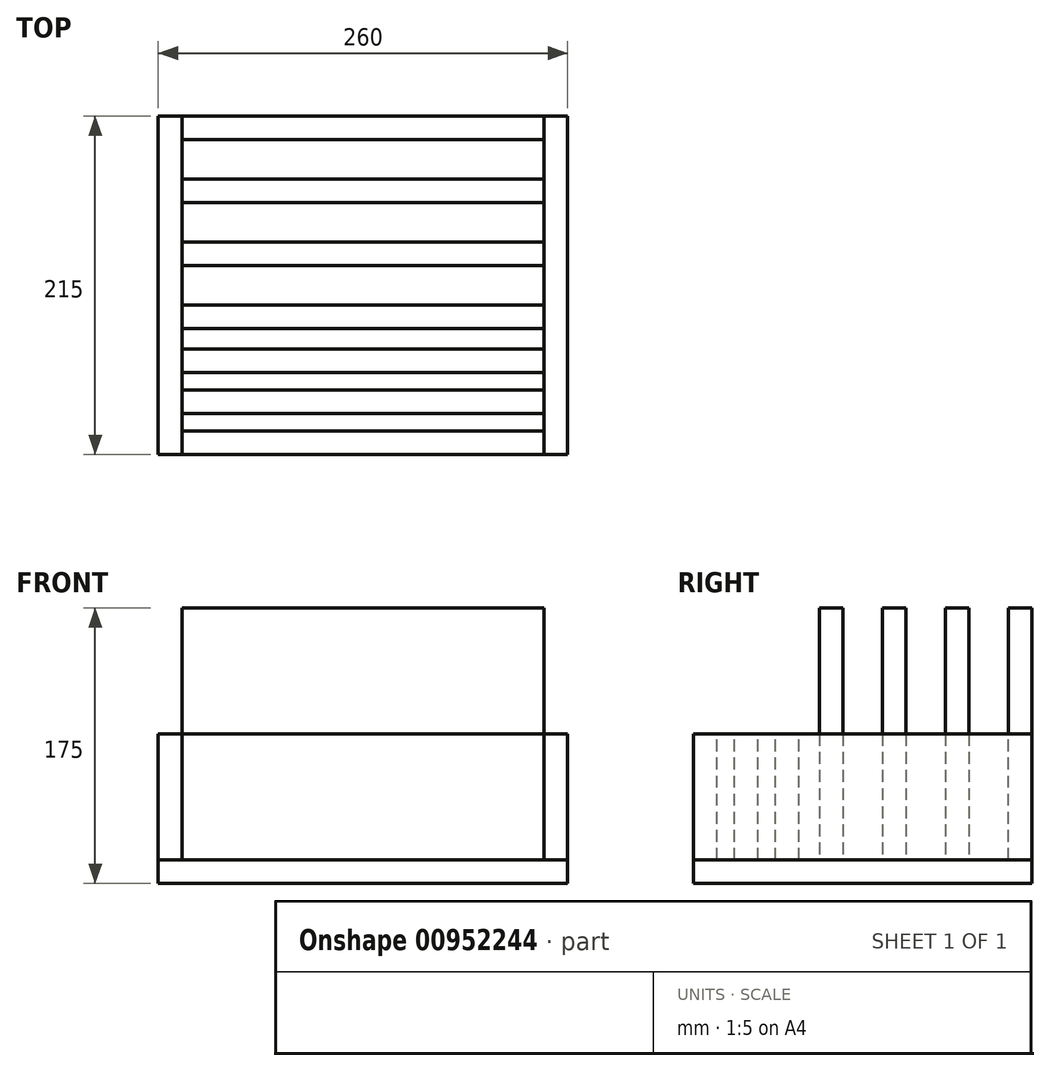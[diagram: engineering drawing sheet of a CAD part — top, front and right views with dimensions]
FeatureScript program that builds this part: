
annotation { "Feature Type Name" : "Feature", "Feature Type Description" : "" }
export const myFeature = defineFeature(function(context is Context, id is Id, definition is map)
    precondition{}
    {
        {
            var Q0;
            Q0=qCreatedBy(makeId("Right.planeOp"),FACE);
            var sketch = newSketch(context, id + "F0", { "sketchPlane" : qUnion([Q0])});
            skLineSegment(sketch, "E0.bottom", {"start": v(-630.81, 4.7) * mm, "end": v(-415.81, 4.7) * mm});
            skLineSegment(sketch, "E0.top", {"start": v(-630.81, -75.3) * mm, "end": v(-415.81, -75.3) * mm});
            skLineSegment(sketch, "E0.left", {"start": v(-630.81, 4.7) * mm, "end": v(-630.81, -75.3) * mm});
            skLineSegment(sketch, "E0.right", {"start": v(-415.81, 4.7) * mm, "end": v(-415.81, -75.3) * mm});
            skSolve(sketch);
        }
        {
            var Q0;
            Q0=makeQuery(id+"F0.imprint","IMPRINT",FACE,{"disambiguationData":[TD([[makeQuery(id+"F0.imprint","IMPRINT",EDGE,{"derivedFrom":sQuery(id+"F0.wireOp",EDGE,"E0.bottom")}),-1.0]])]});
            extrude(context, id + "F1", {"entities" : qUnion([Q0]), "depth" : 15 * mm, "offsetDistance" : 25 * mm});
        }
        {
            var Q0;
            Q0=makeQuery(id+"F1.opExtrude","CAP_FACE",FACE,{"disambiguationData":[OSD([sQuery(id+"F0.wireOp",EDGE,"E0.bottom"),sQuery(id+"F0.wireOp",EDGE,"E0.top"),sQuery(id+"F0.wireOp",EDGE,"E0.left"),sQuery(id+"F0.wireOp",EDGE,"E0.right")])],"isStart":true});
            var sketch = newSketch(context, id + "F2", { "sketchPlane" : qUnion([Q0])});
            skLineSegment(sketch, "E1.bottom", {"start": v(415.81, -75.3) * mm, "end": v(430.81, -75.3) * mm});
            skLineSegment(sketch, "E1.top", {"start": v(415.81, 84.7) * mm, "end": v(430.81, 84.7) * mm});
            skLineSegment(sketch, "E1.left", {"start": v(415.81, -75.3) * mm, "end": v(415.81, 84.7) * mm});
            skLineSegment(sketch, "E1.right", {"start": v(430.81, -75.3) * mm, "end": v(430.81, 84.7) * mm});
            skLineSegment(sketch, "E2.bottom", {"start": v(455.81, 84.7) * mm, "end": v(470.81, 84.7) * mm});
            skLineSegment(sketch, "E2.top", {"start": v(455.81, -75.3) * mm, "end": v(470.81, -75.3) * mm});
            skLineSegment(sketch, "E2.left", {"start": v(455.81, 84.7) * mm, "end": v(455.81, -75.3) * mm});
            skLineSegment(sketch, "E2.right", {"start": v(470.81, 84.7) * mm, "end": v(470.81, -75.3) * mm});
            skLineSegment(sketch, "E3.bottom", {"start": v(495.81, 84.7) * mm, "end": v(510.81, 84.7) * mm});
            skLineSegment(sketch, "E3.top", {"start": v(495.81, -75.3) * mm, "end": v(510.81, -75.3) * mm});
            skLineSegment(sketch, "E3.left", {"start": v(495.81, 84.7) * mm, "end": v(495.81, -75.3) * mm});
            skLineSegment(sketch, "E3.right", {"start": v(510.81, 84.7) * mm, "end": v(510.81, -75.3) * mm});
            skLineSegment(sketch, "E4.bottom", {"start": v(535.81, 84.7) * mm, "end": v(550.81, 84.7) * mm});
            skLineSegment(sketch, "E4.top", {"start": v(535.81, -75.3) * mm, "end": v(550.81, -75.3) * mm});
            skLineSegment(sketch, "E4.left", {"start": v(535.81, 84.7) * mm, "end": v(535.81, -75.3) * mm});
            skLineSegment(sketch, "E4.right", {"start": v(550.81, 84.7) * mm, "end": v(550.81, -75.3) * mm});
            skLineSegment(sketch, "E5.bottom", {"start": v(630.81, -75.3) * mm, "end": v(615.81, -75.3) * mm});
            skLineSegment(sketch, "E5.top", {"start": v(630.81, 4.7) * mm, "end": v(615.81, 4.7) * mm});
            skLineSegment(sketch, "E5.left", {"start": v(630.81, -75.3) * mm, "end": v(630.81, 4.7) * mm});
            skLineSegment(sketch, "E5.right", {"start": v(615.81, -75.3) * mm, "end": v(615.81, 4.7) * mm});
            skLineSegment(sketch, "E6.bottom", {"start": v(604.81, -75.3) * mm, "end": v(589.81, -75.3) * mm});
            skLineSegment(sketch, "E6.top", {"start": v(604.81, 4.7) * mm, "end": v(589.81, 4.7) * mm});
            skLineSegment(sketch, "E6.left", {"start": v(604.81, -75.3) * mm, "end": v(604.81, 4.7) * mm});
            skLineSegment(sketch, "E6.right", {"start": v(589.81, -75.3) * mm, "end": v(589.81, 4.7) * mm});
            skLineSegment(sketch, "E7.bottom", {"start": v(578.81, -75.3) * mm, "end": v(563.81, -75.3) * mm});
            skLineSegment(sketch, "E7.top", {"start": v(578.81, 4.7) * mm, "end": v(563.81, 4.7) * mm});
            skLineSegment(sketch, "E7.left", {"start": v(578.81, -75.3) * mm, "end": v(578.81, 4.7) * mm});
            skLineSegment(sketch, "E7.right", {"start": v(563.81, -75.3) * mm, "end": v(563.81, 4.7) * mm});
            skSolve(sketch);
        }
        {
            var Q0;
            Q0 = qSketchRegion(id + "F2", true);
            extrude(context, id + "F3", {"entities" : qUnion([Q0]), "depth" : 230 * mm, "offsetDistance" : 25 * mm});
        }
        {
            var Q0;
            Q0=qCreatedBy(makeId("Right.planeOp"),FACE);
            cPlane(context, id + "F4", {"entities" : qUnion([Q0]), "cplaneType" : CPlaneType.OFFSET, "offset" : 115 * mm, "oppositeDirection" : true, "width" : 150 * mm, "height" : 150 * mm});
        }
        {
            var Q0;
            Q0=makeQuery(id+"F1.opExtrude","SWEPT_BODY",BODY,{"disambiguationData":[OSD([sQuery(id+"F0.wireOp",EDGE,"E0.bottom"),sQuery(id+"F0.wireOp",EDGE,"E0.top"),sQuery(id+"F0.wireOp",EDGE,"E0.left"),sQuery(id+"F0.wireOp",EDGE,"E0.right")])]});
            var Q1;
            Q1=qCreatedBy(id+"F4.planeOp",FACE);
            mirror(context, id + "F5", {"entities" : qUnion([Q0]), "mirrorPlane" : qUnion([Q1])});
        }
        {
            var Q0;
            Q0=makeQuery(id+"F5.opPattern","COPY",FACE,{"derivedFrom":makeQuery(id+"F1.opExtrude","SWEPT_FACE",FACE,{"disambiguationData":[OSD([sQuery(id+"F0.wireOp",EDGE,"E0.top")])]}),"instanceName":"1"});
            var sketch = newSketch(context, id + "F6", { "sketchPlane" : qUnion([Q0])});
            skLineSegment(sketch, "E8.bottom", {"start": v(-245, 630.81) * mm, "end": v(15, 630.81) * mm});
            skLineSegment(sketch, "E8.top", {"start": v(-245, 415.81) * mm, "end": v(15, 415.81) * mm});
            skLineSegment(sketch, "E8.left", {"start": v(-245, 630.81) * mm, "end": v(-245, 415.81) * mm});
            skLineSegment(sketch, "E8.right", {"start": v(15, 630.81) * mm, "end": v(15, 415.81) * mm});
            skSolve(sketch);
        }
        {
            var Q0;
            {var subQ2=sQuery(id+"F6.wireOp",EDGE,"E8.right");Q0=makeQuery(id+"F6.imprint","IMPRINT",FACE,{"disambiguationData":[TD([[makeQuery(id+"F6.imprint","IMPRINT",EDGE,{"derivedFrom":subQ2}),-1.0]])]});}
            var Q1;
            {var subQ2=sQuery(id+"F6.wireOp",EDGE,"E8.left");Q1=makeQuery(id+"F6.imprint","IMPRINT",FACE,{"disambiguationData":[TD([[makeQuery(id+"F6.imprint","IMPRINT",EDGE,{"derivedFrom":subQ2}),1.0]])]});}
            extrude(context, id + "F7", {"entities" : qUnion([Q0, Q1]), "depth" : 15 * mm, "offsetDistance" : 25 * mm});
        }
    });
